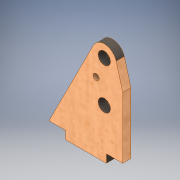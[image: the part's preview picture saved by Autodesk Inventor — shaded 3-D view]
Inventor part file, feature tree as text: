
AUTODESK INVENTOR PART (.ipt)
format: ipt  version: 2019 (Build 230136000, 136)  size: 140,288 bytes
history: native  units: mm
features: extrude x2, sketch x2, other x1
ambient origin geometry x8: Origin, YZ Plane, XZ Plane, XY Plane, X Axis, Y Axis, Z Axis, Center Point
bodies: Body1 (feature_tree)
feature tree (5):
  other  "Твердое тело1"
  extrude  "Выдавливание1"  Depth=6.0mm
  extrude  "Выдавливание2"  Depth=40.0mm
  sketch  "Эскиз1"
  sketch  "Эскиз2"
